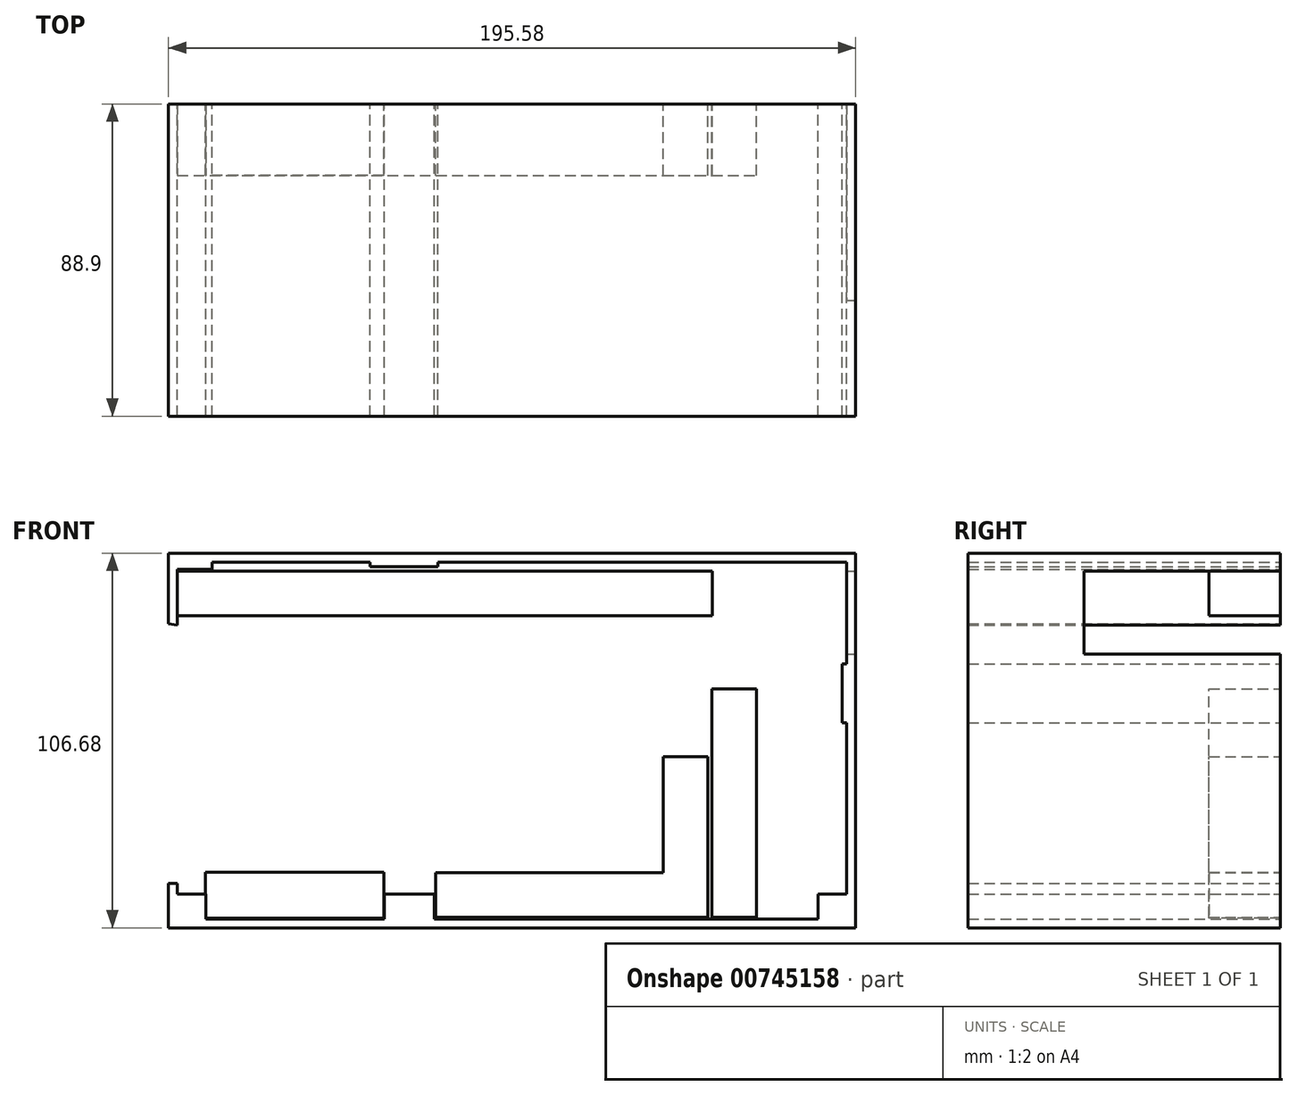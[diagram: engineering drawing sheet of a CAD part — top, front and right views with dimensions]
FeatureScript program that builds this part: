
annotation { "Feature Type Name" : "Feature", "Feature Type Description" : "" }
export const myFeature = defineFeature(function(context is Context, id is Id, definition is map)
    precondition{}
    {
        {
            var Q0;
            Q0=qCreatedBy(makeId("Front.planeOp"),FACE);
            var sketch = newSketch(context, id + "F0", { "sketchPlane" : qUnion([Q0])});
            skLineSegment(sketch, "E0.bottom", {"start": v(-143.65, 50.76) * mm, "end": v(-98.73, 50.76) * mm});
            skLineSegment(sketch, "E0.top", {"start": v(-145.43, -50.84) * mm, "end": v(-94.63, -50.84) * mm});
            skLineSegment(sketch, "E0.left", {"start": v(-153.55, 48.72) * mm, "end": v(-153.55, 32.77) * mm});
            skLineSegment(sketch, "E0.right", {"start": v(36.95, 50.76) * mm, "end": v(36.95, 21.8) * mm});
            skLineSegment(sketch, "E1.0", {"start": v(-156.1, 53.3) * mm, "end": v(39.49, 53.3) * mm});
            skLineSegment(sketch, "E1.1", {"start": v(-156.1, 53.3) * mm, "end": v(-156.1, 33.14) * mm});
            skLineSegment(sketch, "E1.2", {"start": v(-156.1, -53.38) * mm, "end": v(39.49, -53.38) * mm});
            skLineSegment(sketch, "E1.3", {"start": v(39.49, 53.3) * mm, "end": v(39.49, -53.38) * mm});
            skLineSegment(sketch, "E2.top", {"start": v(-153.55, -43.73) * mm, "end": v(-145.43, -43.73) * mm});
            skLineSegment(sketch, "E2.right", {"start": v(-145.43, -50.84) * mm, "end": v(-145.43, -43.73) * mm});
            skLineSegment(sketch, "E3.bottom", {"start": v(-94.63, -43.73) * mm, "end": v(-80.4, -43.73) * mm});
            skLineSegment(sketch, "E3.left", {"start": v(-94.63, -43.73) * mm, "end": v(-94.63, -50.84) * mm});
            skLineSegment(sketch, "E3.right", {"start": v(-80.4, -43.73) * mm, "end": v(-80.4, -50.84) * mm});
            skLineSegment(sketch, "E4.bottom", {"start": v(44.79, -50.84) * mm, "end": v(39.49, -50.84) * mm});
            skPoint(sketch, "E4.top.end.orphan", {"position": v(28.82, -43.73) * mm});
            skLineSegment(sketch, "E5", {"start": v(-153.55, -43.73) * mm, "end": v(-153.55, -40.18) * mm, "construction": true});
            skLineSegment(sketch, "E6.top", {"start": v(-153.55, -40.68) * mm, "end": v(-156.1, -40.68) * mm});
            skLineSegment(sketch, "E7.trimOffspring", {"start": v(-153.55, -40.68) * mm, "end": v(-153.55, -43.73) * mm});
            skLineSegment(sketch, "E8.trimOffspring", {"start": v(-156.1, -40.68) * mm, "end": v(-156.1, -53.38) * mm});
            skLineSegment(sketch, "E9.top", {"start": v(-153.55, 48.72) * mm, "end": v(-143.65, 48.72) * mm});
            skLineSegment(sketch, "E9.right", {"start": v(-143.65, 50.76) * mm, "end": v(-143.65, 48.72) * mm});
            skLineSegment(sketch, "E10.top", {"start": v(-98.73, 49.49) * mm, "end": v(-79.43, 49.49) * mm});
            skLineSegment(sketch, "E10.left", {"start": v(-98.73, 50.76) * mm, "end": v(-98.73, 49.49) * mm});
            skLineSegment(sketch, "E10.right", {"start": v(-79.43, 50.76) * mm, "end": v(-79.43, 49.49) * mm});
            skLineSegment(sketch, "E11.bottom", {"start": v(36.95, 5.04) * mm, "end": v(35.68, 5.04) * mm});
            skLineSegment(sketch, "E11.top", {"start": v(36.95, 21.8) * mm, "end": v(35.68, 21.8) * mm});
            skLineSegment(sketch, "E11.right", {"start": v(35.68, 5.04) * mm, "end": v(35.68, 21.8) * mm});
            skLineSegment(sketch, "E12.top", {"start": v(36.95, -43.73) * mm, "end": v(28.82, -43.73) * mm});
            skLineSegment(sketch, "E12.right", {"start": v(28.82, -50.84) * mm, "end": v(28.82, -43.73) * mm});
            skLineSegment(sketch, "E13", {"start": v(-156.1, 33.14) * mm, "end": v(-153.55, 32.77) * mm});
            skLineSegment(sketch, "E14", {"start": v(36.67, 50.76) * mm, "end": v(36.67, 21.95) * mm, "construction": true});
            skLineSegment(sketch, "E15.trimOffspring", {"start": v(-79.43, 50.76) * mm, "end": v(36.95, 50.76) * mm});
            skLineSegment(sketch, "E16.trimOffspring", {"start": v(-80.4, -50.84) * mm, "end": v(28.82, -50.84) * mm});
            skLineSegment(sketch, "E17.trimOffspring", {"start": v(36.95, 5.04) * mm, "end": v(36.95, -43.73) * mm});
            skLineSegment(sketch, "E18", {"start": v(50.74, -50.84) * mm, "end": v(50.74, -43.73) * mm, "construction": true});
            skLineSegment(sketch, "E19", {"start": v(36.95, 5.04) * mm, "end": v(36.95, -43.73) * mm, "construction": true});
            skLineSegment(sketch, "E20", {"start": v(-145.43, -50.84) * mm, "end": v(-94.63, -50.84) * mm, "construction": true});
            skLineSegment(sketch, "E21", {"start": v(-80.4, -50.84) * mm, "end": v(28.82, -50.84) * mm, "construction": true});
            skPoint(sketch, "E22.start.orphan", {"position": v(-163.42, -40.68) * mm});
            skLineSegment(sketch, "E23", {"start": v(-153.55, 48.72) * mm, "end": v(-153.55, 32.77) * mm, "construction": true});
            skLineSegment(sketch, "E24", {"start": v(-156.1, -50.84) * mm, "end": v(-156.1, -40.68) * mm, "construction": true});
            skSolve(sketch);
        }
        {
            var Q0;
            Q0 = qSketchRegion(id + "F0", true);
            extrude(context, id + "F1", {"entities" : qUnion([Q0]), "depth" : 88.9 * mm, "offsetDistance" : 25.4 * mm});
        }
        {
            var Q0;
            Q0=makeQuery(id+"F1.opExtrude","SWEPT_FACE",FACE,{"disambiguationData":[OSD([sQuery(id+"F0.wireOp",EDGE,"E1.3")])]});
            var sketch = newSketch(context, id + "F2", { "sketchPlane" : qUnion([Q0])});
            skLineSegment(sketch, "E25.bottom", {"start": v(0, 48.18) * mm, "end": v(-55.88, 48.18) * mm});
            skLineSegment(sketch, "E25.top", {"start": v(0, 24.53) * mm, "end": v(-55.88, 24.53) * mm});
            skLineSegment(sketch, "E25.left", {"start": v(0, 48.18) * mm, "end": v(0, 24.53) * mm});
            skLineSegment(sketch, "E25.right", {"start": v(-55.88, 48.18) * mm, "end": v(-55.88, 24.53) * mm});
            skSolve(sketch);
        }
        {
            var Q0;
            Q0 = qSketchRegion(id + "F2", true);
            extrude(context, id + "F3", {"entities" : qUnion([Q0]), "operationType" : NewBodyOperationType.REMOVE, "oppositeDirection" : true, "depth" : 25.4 * mm, "offsetDistance" : 25.4 * mm});
        }
        {
            var Q0;
            Q0=qCreatedBy(makeId("Front.planeOp"),FACE);
            var sketch = newSketch(context, id + "F4", { "sketchPlane" : qUnion([Q0])});
            skLineSegment(sketch, "E26.bottom", {"start": v(-94.81, -37.51) * mm, "end": v(-145.61, -37.51) * mm});
            skLineSegment(sketch, "E26.top", {"start": v(-94.81, -50.58) * mm, "end": v(-145.61, -50.58) * mm});
            skLineSegment(sketch, "E26.left", {"start": v(-94.81, -37.51) * mm, "end": v(-94.81, -50.58) * mm});
            skLineSegment(sketch, "E26.right", {"start": v(-145.61, -37.51) * mm, "end": v(-145.61, -50.58) * mm});
            skPoint(sketch, "E27.left.end.orphan", {"position": v(-79.76, -37.51) * mm});
            skSolve(sketch);
        }
        {
            var Q0;
            Q0=qCreatedBy(makeId("Front.planeOp"),FACE);
            var sketch = newSketch(context, id + "F5", { "sketchPlane" : qUnion([Q0])});
            skLineSegment(sketch, "E28.bottom", {"start": v(-153.68, 48.18) * mm, "end": v(-1.28, 48.18) * mm});
            skLineSegment(sketch, "E28.top", {"start": v(-153.68, 35.48) * mm, "end": v(-1.28, 35.48) * mm});
            skLineSegment(sketch, "E28.left", {"start": v(-153.68, 48.18) * mm, "end": v(-153.68, 35.48) * mm});
            skLineSegment(sketch, "E28.right", {"start": v(-1.28, 48.18) * mm, "end": v(-1.28, 35.48) * mm});
            skSolve(sketch);
        }
        {
            var Q0;
            Q0=qCreatedBy(makeId("Front.planeOp"),FACE);
            var sketch = newSketch(context, id + "F6", { "sketchPlane" : qUnion([Q0])});
            skLineSegment(sketch, "E29.bottom", {"start": v(-80.03, -50.36) * mm, "end": v(-15.25, -50.36) * mm});
            skLineSegment(sketch, "E29.top", {"start": v(-80.03, -37.66) * mm, "end": v(-15.25, -37.66) * mm});
            skLineSegment(sketch, "E29.left", {"start": v(-80.03, -50.36) * mm, "end": v(-80.03, -37.66) * mm});
            skLineSegment(sketch, "E29.right", {"start": v(-15.25, -50.36) * mm, "end": v(-15.25, -37.66) * mm});
            skLineSegment(sketch, "E30.bottom", {"start": v(-15.25, -50.36) * mm, "end": v(-2.55, -50.36) * mm});
            skLineSegment(sketch, "E30.top", {"start": v(-15.25, -4.64) * mm, "end": v(-2.55, -4.64) * mm});
            skLineSegment(sketch, "E30.left", {"start": v(-15.25, -50.36) * mm, "end": v(-15.25, -4.64) * mm});
            skLineSegment(sketch, "E30.right", {"start": v(-2.55, -50.36) * mm, "end": v(-2.55, -4.64) * mm});
            skSolve(sketch);
        }
        {
            var Q0;
            Q0=qCreatedBy(makeId("Front.planeOp"),FACE);
            var sketch = newSketch(context, id + "F7", { "sketchPlane" : qUnion([Q0])});
            skLineSegment(sketch, "E31.bottom", {"start": v(-1.47, -50.36) * mm, "end": v(11.23, -50.36) * mm});
            skLineSegment(sketch, "E31.top", {"start": v(-1.47, 14.69) * mm, "end": v(11.23, 14.69) * mm});
            skLineSegment(sketch, "E31.left", {"start": v(-1.47, -50.36) * mm, "end": v(-1.47, 14.69) * mm});
            skLineSegment(sketch, "E31.right", {"start": v(11.23, -50.36) * mm, "end": v(11.23, 14.69) * mm});
            skSolve(sketch);
        }
        {
            var Q0;
            Q0=makeQuery(id+"F5.imprint","IMPRINT",FACE,{"disambiguationData":[TD([[makeQuery(id+"F5.imprint","IMPRINT",EDGE,{"derivedFrom":sQuery(id+"F5.wireOp",EDGE,"E28.bottom")}),-1.0]])]});
            var Q1;
            Q1=makeQuery(id+"F4.imprint","IMPRINT",FACE,{"disambiguationData":[TD([[makeQuery(id+"F4.imprint","IMPRINT",EDGE,{"derivedFrom":sQuery(id+"F4.wireOp",EDGE,"E26.bottom")}),1.0]])]});
            var Q2;
            {var subQ0=sQuery(id+"F6.wireOp",EDGE,"E29.bottom");Q2=makeQuery(id+"F6.imprint","IMPRINT",FACE,{"disambiguationData":[TD([[makeQuery(id+"F6.imprint","IMPRINT",EDGE,{"derivedFrom":subQ0}),1.0]])]});}
            var Q3;
            {var subQ3=sQuery(id+"F6.wireOp",EDGE,"E30.bottom");Q3=makeQuery(id+"F6.imprint","IMPRINT",FACE,{"disambiguationData":[TD([[makeQuery(id+"F6.imprint","IMPRINT",EDGE,{"derivedFrom":subQ3}),1.0]])]});}
            var Q4;
            Q4=makeQuery(id+"F7.imprint","IMPRINT",FACE,{"disambiguationData":[TD([[makeQuery(id+"F7.imprint","IMPRINT",EDGE,{"derivedFrom":sQuery(id+"F7.wireOp",EDGE,"E31.bottom")}),1.0]])]});
            extrude(context, id + "F8", {"entities" : qUnion([Q0, Q1, Q2, Q3, Q4]), "operationType" : NewBodyOperationType.ADD, "depth" : 20.32 * mm, "offsetDistance" : 25.4 * mm});
        }
    });
